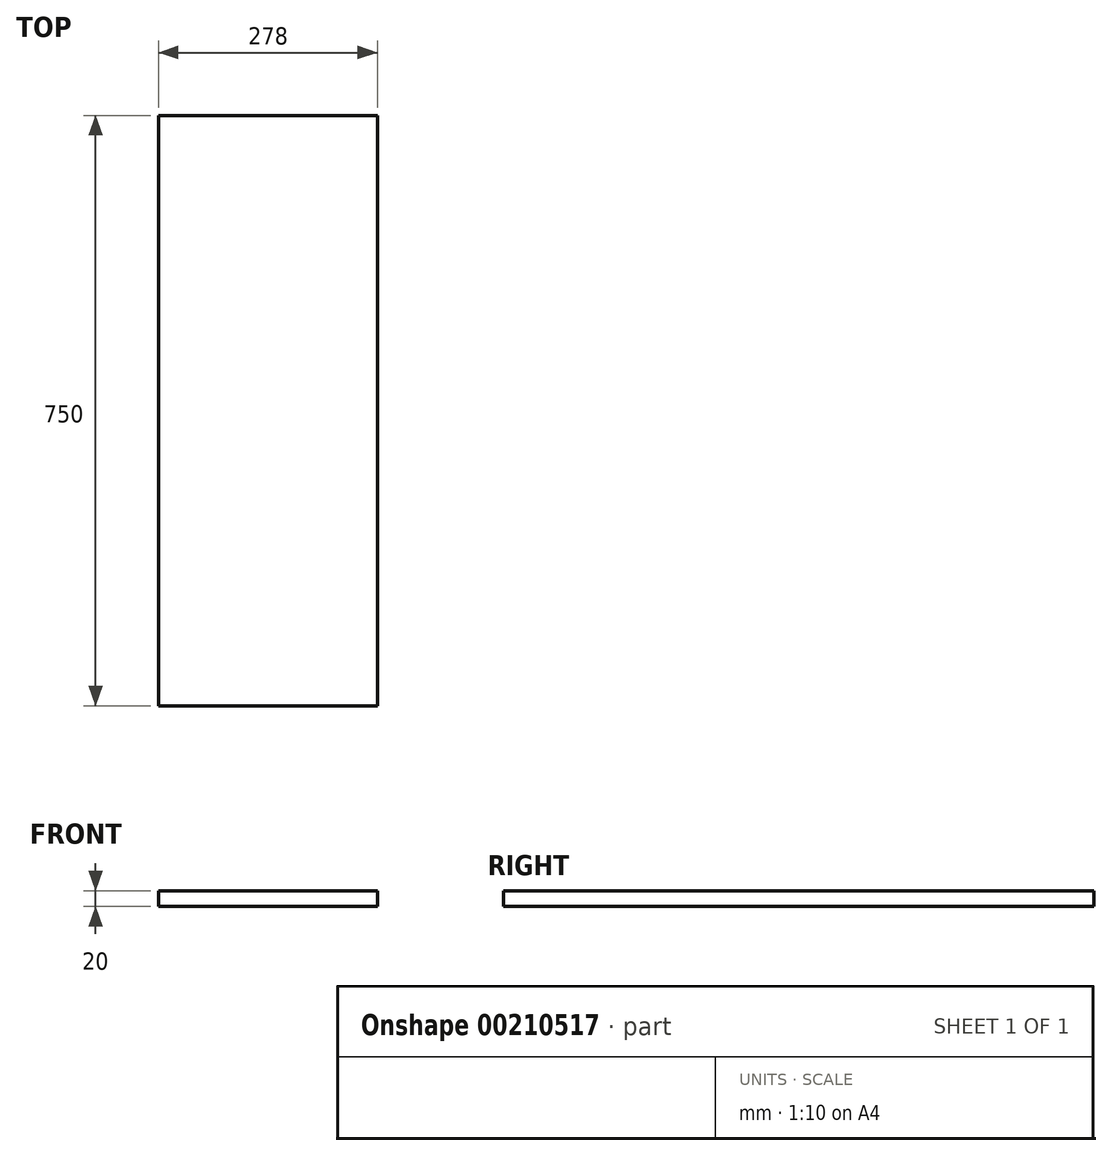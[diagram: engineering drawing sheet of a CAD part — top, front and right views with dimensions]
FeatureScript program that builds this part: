
annotation { "Feature Type Name" : "Feature", "Feature Type Description" : "" }
export const myFeature = defineFeature(function(context is Context, id is Id, definition is map)
    precondition{}
    {
        {
            var Q0;
            Q0=qCreatedBy(makeId("Top.planeOp"),FACE);
            var sketch = newSketch(context, id + "F0", { "sketchPlane" : qUnion([Q0])});
            skLineSegment(sketch, "E0.bottom", {"start": v(-133.15, 647.76) * mm, "end": v(144.85, 647.76) * mm});
            skLineSegment(sketch, "E0.top", {"start": v(-133.15, -102.24) * mm, "end": v(144.85, -102.24) * mm});
            skLineSegment(sketch, "E0.left", {"start": v(-133.15, 647.76) * mm, "end": v(-133.15, -102.24) * mm});
            skLineSegment(sketch, "E0.right", {"start": v(144.85, 647.76) * mm, "end": v(144.85, -102.24) * mm});
            skSolve(sketch);
        }
        {
            var Q0;
            Q0 = qSketchRegion(id + "F0", true);
            extrude(context, id + "F1", {"entities" : qUnion([Q0]), "depth" : 20 * mm});
        }
    });
